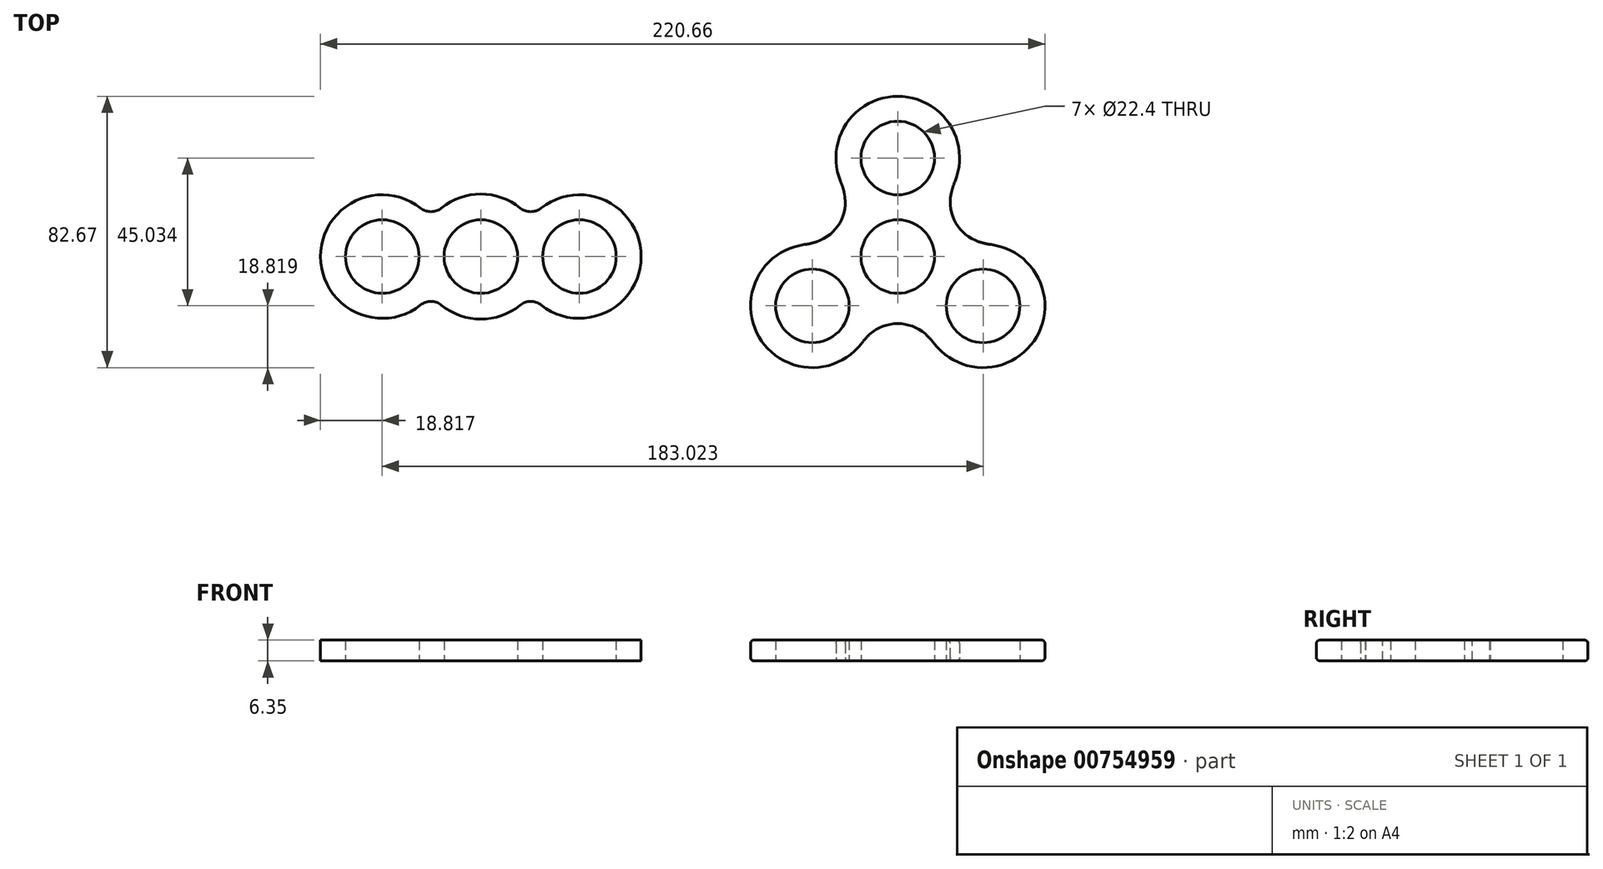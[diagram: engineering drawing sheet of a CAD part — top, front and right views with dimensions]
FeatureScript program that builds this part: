
annotation { "Feature Type Name" : "Feature", "Feature Type Description" : "" }
export const myFeature = defineFeature(function(context is Context, id is Id, definition is map)
    precondition{}
    {
        {
            var Q0;
            Q0=qCreatedBy(makeId("Top.planeOp"),FACE);
            var sketch = newSketch(context, id + "F0", { "sketchPlane" : qUnion([Q0])});
            skArc(sketch, "E0", {"start": v(-11.35, 15.01) * mm, "mid": v(-16.3, 9.41) * mm, "end": v(-18.68, 2.33) * mm});
            skLineSegment(sketch, "E1", {"start": v(0, 0) * mm, "end": v(0, 40.44) * mm, "construction": true});
            skLineSegment(sketch, "E2", {"start": v(0, 0) * mm, "end": v(-35.04, -20.23) * mm, "construction": true});
            skLineSegment(sketch, "E3", {"start": v(0, 0) * mm, "end": v(35.19, -20.32) * mm, "construction": true});
            skArc(sketch, "E4", {"start": v(11.35, 15.01) * mm, "mid": v(0, 48.84) * mm, "end": v(-11.35, 15.01) * mm});
            skCircle(sketch, "E5", {"center": v(0, 0) * mm, "radius": 30.02 * mm, "construction": true});
            skArc(sketch, "E6", {"start": v(7.32, -17.34) * mm, "mid": v(42.3, -24.42) * mm, "end": v(18.68, 2.33) * mm});
            skArc(sketch, "E7", {"start": v(-18.68, 2.33) * mm, "mid": v(-42.3, -24.42) * mm, "end": v(-7.32, -17.34) * mm});
            skCircle(sketch, "E8", {"center": v(0, 30.02) * mm, "radius": 11.2 * mm});
            skCircle(sketch, "E9", {"center": v(26, -15.01) * mm, "radius": 11.2 * mm});
            skCircle(sketch, "E10", {"center": v(-26, -15.01) * mm, "radius": 11.2 * mm});
            skCircle(sketch, "E11", {"center": v(0, 0) * mm, "radius": 11.2 * mm});
            skArc(sketch, "E12.trimOffspring", {"start": v(18.68, 2.33) * mm, "mid": v(16.3, 9.41) * mm, "end": v(11.35, 15.01) * mm});
            skArc(sketch, "E13.trimOffspring", {"start": v(-7.32, -17.34) * mm, "mid": v(0, -18.82) * mm, "end": v(7.32, -17.34) * mm});
            skSolve(sketch);
        }
        {
            var Q0;
            {var subQ0=sQuery(id+"F0.wireOp",EDGE,"E7");var subQ1=sQuery(id+"F0.wireOp",EDGE,"E0");var subQ2=makeQuery(id+"F0.imprint","INTERSECT",VERTEX,{"disambiguationData":[OD(0.0)],"derivedFrom":[subQ1,subQ0]});Q0=makeQuery(id+"F0.imprint","IMPRINT",FACE,{"disambiguationData":[TD([[makeQuery(id+"F0.imprint","IMPRINT",EDGE,{"disambiguationData":[TD([[subQ2,-1.0]])],"derivedFrom":subQ1}),-1.0]])]});}
            var Q1;
            {var subQ0=sQuery(id+"F0.wireOp",EDGE,"E4");var subQ1=sQuery(id+"F0.wireOp",EDGE,"E0");var subQ2=makeQuery(id+"F0.imprint","INTERSECT",VERTEX,{"disambiguationData":[OD(0.0)],"derivedFrom":[subQ1,subQ0]});Q1=makeQuery(id+"F0.imprint","IMPRINT",FACE,{"disambiguationData":[TD([[makeQuery(id+"F0.imprint","IMPRINT",EDGE,{"disambiguationData":[TD([[subQ2,1.0]])],"derivedFrom":subQ1}),1.0]])]});}
            var Q2;
            {var subQ0=sQuery(id+"F0.wireOp",EDGE,"E7");var subQ1=sQuery(id+"F0.wireOp",EDGE,"E0");var subQ2=makeQuery(id+"F0.imprint","INTERSECT",VERTEX,{"disambiguationData":[OD(0.0)],"derivedFrom":[subQ1,subQ0]});Q2=makeQuery(id+"F0.imprint","IMPRINT",FACE,{"disambiguationData":[TD([[makeQuery(id+"F0.imprint","IMPRINT",EDGE,{"disambiguationData":[TD([[subQ2,-1.0]])],"derivedFrom":subQ1}),1.0]])]});}
            var Q3;
            {var subQ0=sQuery(id+"F0.wireOp",EDGE,"E4");var subQ1=sQuery(id+"F0.wireOp",EDGE,"E0");var subQ2=makeQuery(id+"F0.imprint","INTERSECT",VERTEX,{"disambiguationData":[OD(0.0)],"derivedFrom":[subQ1,subQ0]});Q3=makeQuery(id+"F0.imprint","IMPRINT",FACE,{"disambiguationData":[TD([[makeQuery(id+"F0.imprint","IMPRINT",EDGE,{"disambiguationData":[TD([[subQ2,-1.0]])],"derivedFrom":subQ1}),1.0]])]});}
            var Q4;
            {var subQ0=sQuery(id+"F0.wireOp",EDGE,"E4");var subQ1=sQuery(id+"F0.wireOp",EDGE,"E0");var subQ2=makeQuery(id+"F0.imprint","INTERSECT",VERTEX,{"disambiguationData":[OD(0.0)],"derivedFrom":[subQ1,subQ0]});Q4=makeQuery(id+"F0.imprint","IMPRINT",FACE,{"disambiguationData":[TD([[makeQuery(id+"F0.imprint","IMPRINT",EDGE,{"disambiguationData":[TD([[subQ2,-1.0]])],"derivedFrom":subQ1}),-1.0]])]});}
            var Q5;
            {var subQ0=sQuery(id+"F0.wireOp",EDGE,"E6");var subQ1=sQuery(id+"F0.wireOp",EDGE,"E0");var subQ2=makeQuery(id+"F0.imprint","INTERSECT",VERTEX,{"disambiguationData":[OD(0.0)],"derivedFrom":[subQ1,subQ0]});Q5=makeQuery(id+"F0.imprint","IMPRINT",FACE,{"disambiguationData":[TD([[makeQuery(id+"F0.imprint","IMPRINT",EDGE,{"disambiguationData":[TD([[subQ2,1.0]])],"derivedFrom":subQ1}),-1.0]])]});}
            var Q6;
            {var subQ0=sQuery(id+"F0.wireOp",EDGE,"E6");var subQ1=sQuery(id+"F0.wireOp",EDGE,"E0");var subQ2=makeQuery(id+"F0.imprint","INTERSECT",VERTEX,{"disambiguationData":[OD(0.0)],"derivedFrom":[subQ1,subQ0]});Q6=makeQuery(id+"F0.imprint","IMPRINT",FACE,{"disambiguationData":[TD([[makeQuery(id+"F0.imprint","IMPRINT",EDGE,{"disambiguationData":[TD([[subQ2,1.0]])],"derivedFrom":subQ1}),1.0]])]});}
            extrude(context, id + "F1", {"entities" : qUnion([Q0, Q1, Q2, Q3, Q4, Q5, Q6]), "depth" : 6.35 * mm, "offsetDistance" : 25.4 * mm});
        }
        {
            var Q0;
            {var subQ0=sQuery(id+"F0.wireOp",EDGE,"E7");var subQ1=sQuery(id+"F0.wireOp",EDGE,"E0");Q0=makeQuery(id+"F1.opExtrude","SWEPT_EDGE",EDGE,{"disambiguationData":[OSD([subQ1,subQ0]),TDD([makeQuery(id+"F0.imprint","INTERSECT",VERTEX,{"disambiguationData":[OD(1.0)],"derivedFrom":[subQ1,subQ0]})])]});}
            var Q1;
            {var subQ0=sQuery(id+"F0.wireOp",EDGE,"E6");var subQ1=sQuery(id+"F0.wireOp",EDGE,"E0");Q1=makeQuery(id+"F1.opExtrude","SWEPT_EDGE",EDGE,{"disambiguationData":[OSD([subQ1,subQ0]),TDD([makeQuery(id+"F0.imprint","INTERSECT",VERTEX,{"disambiguationData":[OD(1.0)],"derivedFrom":[subQ1,subQ0]})])]});}
            var Q2;
            {var subQ0=sQuery(id+"F0.wireOp",EDGE,"E6");var subQ1=sQuery(id+"F0.wireOp",EDGE,"E0");Q2=makeQuery(id+"F1.opExtrude","SWEPT_EDGE",EDGE,{"disambiguationData":[OSD([subQ1,subQ0]),TDD([makeQuery(id+"F0.imprint","INTERSECT",VERTEX,{"disambiguationData":[OD(0.0)],"derivedFrom":[subQ1,subQ0]})])]});}
            var Q3;
            {var subQ0=sQuery(id+"F0.wireOp",EDGE,"E4");var subQ1=sQuery(id+"F0.wireOp",EDGE,"E0");Q3=makeQuery(id+"F1.opExtrude","SWEPT_EDGE",EDGE,{"disambiguationData":[OSD([subQ1,subQ0]),TDD([makeQuery(id+"F0.imprint","INTERSECT",VERTEX,{"disambiguationData":[OD(0.0)],"derivedFrom":[subQ1,subQ0]})])]});}
            var Q4;
            {var subQ0=sQuery(id+"F0.wireOp",EDGE,"E4");var subQ1=sQuery(id+"F0.wireOp",EDGE,"E0");Q4=makeQuery(id+"F1.opExtrude","SWEPT_EDGE",EDGE,{"disambiguationData":[OSD([subQ1,subQ0]),TDD([makeQuery(id+"F0.imprint","INTERSECT",VERTEX,{"disambiguationData":[OD(1.0)],"derivedFrom":[subQ1,subQ0]})])]});}
            var Q5;
            {var subQ0=sQuery(id+"F0.wireOp",EDGE,"E7");var subQ1=sQuery(id+"F0.wireOp",EDGE,"E0");Q5=makeQuery(id+"F1.opExtrude","SWEPT_EDGE",EDGE,{"disambiguationData":[OSD([subQ1,subQ0]),TDD([makeQuery(id+"F0.imprint","INTERSECT",VERTEX,{"disambiguationData":[OD(0.0)],"derivedFrom":[subQ1,subQ0]})])]});}
            var Q6;
            Q6=makeQuery(id+"F1.opExtrude","SWEPT_EDGE",EDGE,{"disambiguationData":[OSD([sQuery(id+"F0.wireOp",EDGE,"E7"),sQuery(id+"F0.wireOp",EDGE,"E13.trimOffspring")])]});
            var Q7;
            Q7=makeQuery(id+"F1.opExtrude","SWEPT_EDGE",EDGE,{"disambiguationData":[OSD([sQuery(id+"F0.wireOp",EDGE,"E4"),sQuery(id+"F0.wireOp",EDGE,"E12.trimOffspring")])]});
            fillet(context, id + "F2", {"entities" : qUnion([Q0, Q1, Q2, Q3, Q4, Q5, Q6, Q7]), "radius" : 20.32 * mm, "tangentPropagation" : true, "allowEdgeOverflow" : false});
        }
        {
            var Q0;
            {var subQ0=sQuery(id+"F0.wireOp",EDGE,"E12.trimOffspring");Q0=makeQuery(id+"F2.opFillet","BLEND_EDGE",EDGE,{"blendedFrom":[makeQuery(id+"F1.opExtrude","SWEPT_EDGE",EDGE,{"disambiguationData":[OSD([sQuery(id+"F0.wireOp",EDGE,"E4"),subQ0])]}),makeQuery(id+"F1.opExtrude","SWEPT_EDGE",EDGE,{"disambiguationData":[OSD([sQuery(id+"F0.wireOp",EDGE,"E6"),subQ0])]})],"blendedInto":[]});}
            var Q1;
            {var subQ0=sQuery(id+"F0.wireOp",EDGE,"E13.trimOffspring");Q1=makeQuery(id+"F2.opFillet","BLEND_EDGE",EDGE,{"blendedFrom":[makeQuery(id+"F1.opExtrude","SWEPT_EDGE",EDGE,{"disambiguationData":[OSD([sQuery(id+"F0.wireOp",EDGE,"E6"),subQ0])]}),makeQuery(id+"F1.opExtrude","SWEPT_EDGE",EDGE,{"disambiguationData":[OSD([sQuery(id+"F0.wireOp",EDGE,"E7"),subQ0])]})],"blendedInto":[]});}
            var Q2;
            {var subQ0=sQuery(id+"F0.wireOp",EDGE,"E0");Q2=makeQuery(id+"F2.opFillet","BLEND_EDGE",EDGE,{"blendedFrom":[makeQuery(id+"F1.opExtrude","SWEPT_EDGE",EDGE,{"disambiguationData":[OSD([subQ0,sQuery(id+"F0.wireOp",EDGE,"E4")])]}),makeQuery(id+"F1.opExtrude","SWEPT_EDGE",EDGE,{"disambiguationData":[OSD([subQ0,sQuery(id+"F0.wireOp",EDGE,"E7")])]})],"blendedInto":[]});}
            fillet(context, id + "F3", {"entities" : qUnion([Q0, Q1, Q2]), "radius" : 12.7 * mm, "tangentPropagation" : true, "allowEdgeOverflow" : false});
        }
        {
            var Q0;
            Q0=qCreatedBy(makeId("Top.planeOp"),FACE);
            var sketch = newSketch(context, id + "F4", { "sketchPlane" : qUnion([Q0])});
            skPoint(sketch, "E14", {"position": v(-127, 0) * mm});
            skLineSegment(sketch, "E15", {"start": v(-127, 0) * mm, "end": v(-127, 18.6) * mm, "construction": true});
            skLineSegment(sketch, "E16", {"start": v(-62.3, 0) * mm, "end": v(-127, 0) * mm, "construction": true});
            skCircle(sketch, "E17", {"center": v(-127, 0) * mm, "radius": 11.2 * mm});
            skArc(sketch, "E18", {"start": v(-111.84, 11.54) * mm, "mid": v(-127, 19.05) * mm, "end": v(-142.16, 11.54) * mm});
            skCircle(sketch, "E19", {"center": v(-96.98, 0) * mm, "radius": 11.2 * mm});
            skArc(sketch, "E20", {"start": v(-111.84, -11.54) * mm, "mid": v(-78.16, 0) * mm, "end": v(-111.84, 11.54) * mm});
            skArc(sketch, "E21.MirrorCS", {"start": v(-142.16, -11.54) * mm, "mid": v(-175.84, 0) * mm, "end": v(-142.16, 11.54) * mm});
            skCircle(sketch, "E22.MirrorC", {"center": v(-157.02, 0) * mm, "radius": 11.2 * mm});
            skArc(sketch, "E23.trimOffspring", {"start": v(-142.16, -11.54) * mm, "mid": v(-127, -19.05) * mm, "end": v(-111.84, -11.54) * mm});
            skSolve(sketch);
        }
        {
            var Q0;
            Q0=makeQuery(id+"F4.imprint","IMPRINT",FACE,{"disambiguationData":[TD([[makeQuery(id+"F4.imprint","IMPRINT",EDGE,{"derivedFrom":sQuery(id+"F4.wireOp",EDGE,"E17")}),-1.0]])]});
            extrude(context, id + "F5", {"entities" : qUnion([Q0]), "depth" : 6.35 * mm, "offsetDistance" : 25.4 * mm});
        }
        {
            var Q0;
            Q0=makeQuery(id+"F5.opExtrude","SWEPT_EDGE",EDGE,{"disambiguationData":[OSD([sQuery(id+"F4.wireOp",EDGE,"E21.MirrorCS"),sQuery(id+"F4.wireOp",EDGE,"E23.trimOffspring")])]});
            var Q1;
            Q1=makeQuery(id+"F5.opExtrude","SWEPT_EDGE",EDGE,{"disambiguationData":[OSD([sQuery(id+"F4.wireOp",EDGE,"E20"),sQuery(id+"F4.wireOp",EDGE,"E23.trimOffspring")])]});
            var Q2;
            Q2=makeQuery(id+"F5.opExtrude","SWEPT_EDGE",EDGE,{"disambiguationData":[OSD([sQuery(id+"F4.wireOp",EDGE,"E18"),sQuery(id+"F4.wireOp",EDGE,"E20")])]});
            var Q3;
            Q3=makeQuery(id+"F5.opExtrude","SWEPT_EDGE",EDGE,{"disambiguationData":[OSD([sQuery(id+"F4.wireOp",EDGE,"E18"),sQuery(id+"F4.wireOp",EDGE,"E21.MirrorCS")])]});
            fillet(context, id + "F6", {"entities" : qUnion([Q0, Q1, Q2, Q3]), "radius" : 5.08 * mm, "tangentPropagation" : true, "allowEdgeOverflow" : false});
        }
        {
            var Q0;
            Q0=makeQuery(id+"F1.opExtrude","CAP_EDGE",EDGE,{"disambiguationData":[OSD([sQuery(id+"F0.wireOp",EDGE,"E7")])],"isStart":false});
            var Q1;
            Q1=makeQuery(id+"F1.opExtrude","CAP_EDGE",EDGE,{"disambiguationData":[OSD([sQuery(id+"F0.wireOp",EDGE,"E7")])],"isStart":true});
            fillet(context, id + "F7", {"entities" : qUnion([Q0, Q1]), "radius" : 1.02 * mm, "tangentPropagation" : true, "allowEdgeOverflow" : false});
        }
    });
